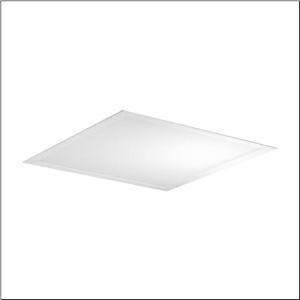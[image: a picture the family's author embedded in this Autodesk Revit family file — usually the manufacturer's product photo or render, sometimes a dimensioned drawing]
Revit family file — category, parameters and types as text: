
# Revit family: apollon_r__31_square_51mp11w72342_58c9
name_source: partatom
category: Lighting Fixtures
units: mm (PartAtom-declared; Revit-internal decimal feet)

## family parameters
Cut with Voids When Loaded = No
Host = Face
Light Source = No
Part Type = Normal
Room Calculation Point = No
Round Connector Dimension = Use Diameter
Shared = No

## types (1)
- Apollon® 31 square (1 x LED, 3800 lm, 27.5 W, 3000K)
    Apparent Load = 28 VA
    CIE Flux Codes = 61 87 97 100 100
    Color Rendering = 80
    Color Temperature = 3000K
    Default Elevation = 1800 mm
    Description = Apollon® 31 square, office luminaire, primary optical cover: micro prismatic cover, of PMMA, CAT 2 (L<= 3000cd/m²), light emission: direct distribution, primary light characteristic: symmetric, installation type: lay-in mounting, LED, rated luminous flux: 3.800lm, luminous efficacy: 138lm/W, light colour: 830, colour temperature: 3000K, with terminal, 3-pole, mains connection: 220..240V, AC, 50/60Hz, rated input power: 28W, housing, of aluminium, traffic white (RAL 9016), module: M625, length: 620mm, width: 620mm, height: 32mm, housing upper side, of sheet steel, galvanised, protection rating (complete): IP20, protection rating (on room side): IP40, insulation class (complete): insulation class II (safety insulation), certification: CE, ENEC, impact resistance: IK03, permissible operating ambient temperature: -20..+40°C, permissible storage temperature: -20..+60°C, packaging unit: 1 piece
    Height = 0 mm  [stored 0 ft]
    Lamp = 1 x LED
    Lamp Light Flux = 3800 lm
    Lamp Power = 27.5 W
    Lamp count = 1
    Length = 620 mm
    Luminous efficacy = 138 lm/W
    Manufacturer = Siteco
    ModVariant = No
    Model = 51MP11W72342
    Mounting Place = Ceiling
    Mounting Type = Recessed
    Number of Poles = 1
    OnlyDefault = Yes
    Power Factor = 1
    Product Name = Apollon® 31 square
    Product group = office luminaire | ceiling recessed
    ProductGroupID = 401
    Protection Class = Protection class II
    Protection Degree = IP 20
    RLX_Detail_Level = 1
    RLX_Emergency_Light_Flux = 0 lm
    RLX_Emergency_Type = 0
    RLX_Emergency_Type_DB = No
    RlxData = <blob elided: 12937 chars, md5=0b90f5f1>
    Socket = socket
    Standby Power = 0 W
    System Light Flux = 3800 lm
    System Power = 28 W
    Type Comments = Product without accessories
    Type Image = l_1291039.jpg
    URL = http://relux.com
    VarID = ---
    Voltage = 0 V
    Weight = 0.00 kg
    Width = 620 mm

note: [stored X ft] marks values corroborated as IEEE doubles in the binary element streams (Revit-internal decimal feet)

## geometry (parser evidence)
native form markers: Sweep x8
no freeform markers — native parametric forms only
